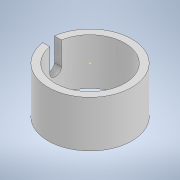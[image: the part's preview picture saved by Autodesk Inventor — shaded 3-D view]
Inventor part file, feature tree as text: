
AUTODESK INVENTOR PART (.ipt)
format: ipt  version: 2022.1 (Build 261234000, 234)  size: 120,320 bytes
history: native  units: in
note: dims shown in document units (in); Inventor stores cm internally (conversion verified against a paired STEP export)
features: sketch x5, extrude x2
ambient origin geometry x8: Origin, YZ Plane, XZ Plane, XY Plane, X Axis, Y Axis, Z Axis, Center Point
bodies: Solid1 (feature_tree)
feature tree (7):
  extrude  "Extrusion1"  Depth=0.9in
  sketch  "3D Sketch1"
  sketch  "3D Sketch2"
  sketch  "Sketch2"  dims[d2=0.5in d3=0.0in d4=0.125in]
  extrude  "Extrusion2"  Depth=0.125in
  sketch  "Sketch1"  dims[d0=0.75in d1=0.9in]
  sketch  "Sketch3"  dims[d5=0.25in d6=0.5in d7=0.0in]
